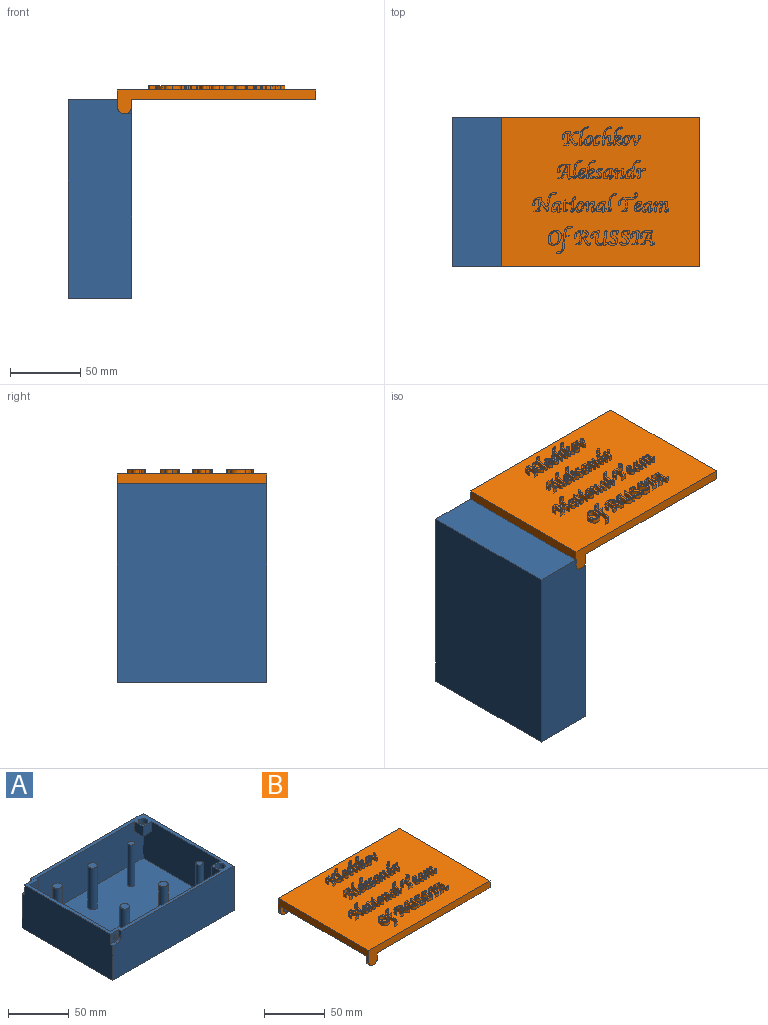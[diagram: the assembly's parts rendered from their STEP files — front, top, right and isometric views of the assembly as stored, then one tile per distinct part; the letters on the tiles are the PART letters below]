
ASSEMBLY  parts=2 mates=1
PART A: 53 faces, bbox 141x106x45 mm
  f0: plane 106x45mm, normal (-1,0,0), area 4710.1mm2, adj f1,f10,f11,f12,f29,f32,f47,f50
  f1: plane 141x106mm, normal (0,0,1), area 1548.2mm2, adj f0,f2,f3,f4,f5,f6,f7,f8
  f2: plane 100x42mm, normal (1,0,0), area 4137.9mm2, adj f1,f3,f4,f35,f36,f38,f43,f44
  f3: plane 135x42mm, normal (0,-1,0), area 5469.5mm2, adj f1,f2,f9,f26,f37,f38,f44,f45
  f4: plane 135x42mm, normal (0,1,0), area 5469.5mm2, adj f1,f2,f9,f27,f38,f39,f41,f42
  f5: cylinder r=4mm len=8mm, axis (0,0,-1), area 125.7mm2, adj f1,f40
  f6: plane 10x10mm, normal (0,1,0), area 100mm2, adj f1,f9,f27,f39
  f7: plane 10x10mm, normal (0,-1,0), area 100mm2, adj f1,f9,f26,f37
  f8: cylinder r=4mm len=8mm, axis (0,0,-1), area 125.7mm2, adj f1,f28
  f9: plane 100x42mm, normal (-1,0,0), area 4000mm2, adj f1,f3,f4,f6,f7,f37,f38,f39
  f10: plane 141x45mm, normal (0,1,0), area 6250.8mm2, adj f0,f1,f12,f13,f32,f33,f34
  f11: plane 141x45mm, normal (0,-1,0), area 6250.8mm2, adj f0,f1,f12,f13,f29,f30,f31
  f12: plane 141x106mm, normal (0,0,-1), area 14946mm2, adj f0,f10,f11,f13
  f13: plane 106x45mm, normal (1,0,0), area 4770mm2, adj f1,f10,f11,f12
  f14: plane 7.9x7.9mm, normal (0,0,1), area 49mm2, adj f15
  f15: cylinder r=3.95mm len=42mm, axis (0,0,-1), area 1042.4mm2, adj f14,f38
  f16: plane 7.9x7.9mm, normal (0,0,1), area 49mm2, adj f17
  f17: cylinder r=3.95mm len=42mm, axis (0,0,-1), area 1042.4mm2, adj f16,f38
  f18: plane 7.9x7.9mm, normal (0,0,1), area 49mm2, adj f19
  f19: cylinder r=3.95mm len=42mm, axis (0,0,-1), area 1042.4mm2, adj f18,f38
  f20: plane 5.9x5.9mm, normal (0,0,1), area 27.3mm2, adj f21
  f21: cylinder r=2.95mm len=42mm, axis (0,0,-1), area 778.5mm2, adj f20,f38
  f22: plane 7.9x7.9mm, normal (0,0,1), area 49mm2, adj f23
  f23: cylinder r=3.95mm len=42mm, axis (0,0,-1), area 1042.4mm2, adj f22,f38
  f24: plane 5.9x5.9mm, normal (0,0,1), area 27.3mm2, adj f25
  f25: cylinder r=2.95mm len=42mm, axis (0,0,-1), area 778.5mm2, adj f24,f38
  f26: plane 10x10mm, normal (-1,0,0), area 100mm2, adj f1,f3,f7,f37
  f27: plane 10x10mm, normal (-1,0,0), area 100mm2, adj f1,f4,f6,f39
  f28: plane 8x8mm, normal (0,0,1), area 50.3mm2, adj f8
  f29: plane 5.33x3mm, normal (0,0,1), area 16mm2, adj f0,f11,f30,f50
  f30: cylinder r=5mm len=5.13mm, axis (0,-1,0), area 23mm2, adj f11,f29,f31,f50
  f31: plane 4.86x3mm, normal (-1,0,-0.03), area 14.6mm2, adj f1,f11,f30,f50
  f32: plane 5.33x3mm, normal (0,0,1), area 16mm2, adj f0,f10,f34,f47
  f33: plane 4.86x3mm, normal (-1,0,-0.03), area 14.6mm2, adj f1,f10,f34,f47
  f34: cylinder r=5mm len=5.13mm, axis (0,1,0), area 23mm2, adj f10,f32,f33,f47
  f35: plane 10.34x10.31mm, normal (0,-1,0), area 100.5mm2, adj f1,f2,f44,f45,f46
  f36: plane 10.34x10.31mm, normal (0,1,0), area 100.5mm2, adj f1,f2,f41,f42,f43
  f37: plane 10x10mm, normal (0,0,-1), area 100mm2, adj f3,f7,f9,f26
  f38: plane 135x100mm, normal (0,0,1), area 13249.3mm2, adj f2,f3,f4,f9,f15,f17,f19,f21
  f39: plane 10x10mm, normal (0,0,-1), area 100mm2, adj f4,f6,f9,f27
  f40: plane 8x8mm, normal (0,0,1), area 50.3mm2, adj f5
  f41: plane 5x3mm, normal (1,0,0), area 15mm2, adj f1,f4,f36,f42
  f42: cylinder r=5.34mm len=5.34mm, axis (0,1,0), area 25.2mm2, adj f4,f36,f41,f43
  f43: plane 4.97x3mm, normal (0,0,-1), area 14.9mm2, adj f2,f4,f36,f42
  f44: plane 4.97x3mm, normal (0,0,-1), area 14.9mm2, adj f2,f3,f35,f45
  f45: cylinder r=5.34mm len=5.34mm, axis (0,-1,0), area 25.2mm2, adj f3,f35,f44,f46
  f46: plane 5x3mm, normal (1,0,0), area 15mm2, adj f1,f3,f35,f45
  f47: plane 10x9.99mm, normal (0,1,0), area 81.7mm2, adj f0,f1,f32,f33,f34,f49
  f48: plane 4x4mm, normal (0,1,0), area 12.6mm2, adj f49
  f49: cylinder r=2mm len=4mm, axis (0,1,0), area 18.8mm2, adj f47,f48
  f50: plane 10x9.99mm, normal (0,-1,0), area 81.7mm2, adj f0,f1,f29,f30,f31,f52
  f51: plane 4x4mm, normal (0,-1,0), area 12.6mm2, adj f52
  f52: cylinder r=2mm len=4mm, axis (0,-1,0), area 18.8mm2, adj f50,f51
PART B: 222 faces, bbox 141x106x20 mm
  f0: plane 141x106mm, normal (0,0,1), area 13851.5mm2, adj f6,f7,f8,f11,f32,f33,f34,f35
  f1: plane 100x3mm, normal (0,0,-1), area 300mm2, adj f8,f20,f22,f27
  f2: plane 131.14x106mm, normal (0,0,-1), area 1297.1mm2, adj f3,f6,f7,f9,f11,f13,f14,f16
  f3: plane 11.79x4mm, normal (-1,0,0), area 47.1mm2, adj f2,f22,f23,f26
  f4: plane 3x0.66mm, normal (0,0,-1), area 2mm2, adj f6,f10,f19,f20
  f5: plane 3x0.66mm, normal (0,0,-1), area 2mm2, adj f7,f12,f18,f22
  f6: plane 141x16.99mm, normal (0,1,0), area 1075.9mm2, adj f0,f2,f4,f8,f9,f10,f11,f19
  f7: plane 141x16.99mm, normal (0,-1,0), area 1075.9mm2, adj f0,f2,f5,f8,f11,f12,f13,f18
  f8: plane 106x12mm, normal (-1,0,0), area 772mm2, adj f0,f1,f6,f7,f18,f19,f20,f22
  f9: plane 4.86x3mm, normal (1,0,0.03), area 14.6mm2, adj f2,f6,f10,f20
  f10: cylinder r=5mm len=5.13mm, axis (0,-1,0), area 23mm2, adj f4,f6,f9,f20
  f11: plane 106x7mm, normal (1,0,0), area 742mm2, adj f0,f2,f6,f7
  f12: cylinder r=5mm len=5.13mm, axis (0,1,0), area 23mm2, adj f5,f7,f13,f22
  f13: plane 4.86x3mm, normal (1,0,0.03), area 14.6mm2, adj f2,f7,f12,f22
  f14: cylinder r=4mm len=8mm, axis (0,0,-1), area 125.7mm2, adj f2,f15
  f15: plane 8x8mm, normal (0,0,-1), area 50.3mm2, adj f14
  f16: cylinder r=4mm len=8mm, axis (0,0,-1), area 125.7mm2, adj f2,f17
  f17: plane 8x8mm, normal (0,0,-1), area 50.3mm2, adj f16
  f18: cylinder r=5mm len=4.99mm, axis (0,1,0), area 22.6mm2, adj f5,f7,f8,f22
  f19: cylinder r=5mm len=4.99mm, axis (0,1,0), area 22.6mm2, adj f4,f6,f8,f20
  f20: plane 124.82x13.99mm, normal (0,-1,0), area 563.6mm2, adj f1,f2,f4,f8,f9,f10,f19,f21
  f21: plane 11.79x4mm, normal (-1,0,0), area 47.1mm2, adj f2,f20,f23,f24
  f22: plane 124.82x13.99mm, normal (0,1,0), area 563.6mm2, adj f1,f2,f3,f5,f8,f12,f13,f18
  f23: plane 135x100mm, normal (0,0,-1), area 13189.2mm2, adj f3,f20,f21,f22,f24,f25,f26,f27
  f24: plane 13.19x4mm, normal (0,-1,0), area 52.7mm2, adj f2,f21,f23,f25
  f25: plane 76.43x4mm, normal (-1,0,0), area 305.7mm2, adj f2,f23,f24,f26
  f26: plane 13.19x4mm, normal (0,1,0), area 52.7mm2, adj f2,f3,f23,f25
  f27: plane 100x4mm, normal (1,0,0), area 400mm2, adj f1,f20,f22,f23
  f28: plane 4x4mm, normal (0,1,0), area 12.6mm2, adj f29
  f29: cylinder r=2mm len=4mm, axis (0,-1,0), area 18.8mm2, adj f22,f28
  f30: plane 4x4mm, normal (0,-1,0), area 12.6mm2, adj f31
  f31: cylinder r=2mm len=4mm, axis (0,1,0), area 18.8mm2, adj f20,f30
  f32: plane 3x0.46mm, normal (0,-1,0), area 1.4mm2, adj f0,f33,f45,f46
  f33: extruded ~9.8x6.28mm, area 97.6mm2, adj f0,f32,f34,f46
  f34: plane 3.88x3mm, normal (1,-0.07,0), area 11.7mm2, adj f0,f33,f35,f46
  f35: extruded ~5.75x5.6mm, area 34.6mm2, adj f0,f34,f36,f46
  f36: extruded ~3.07x3mm, area 14.9mm2, adj f0,f35,f37,f46
  f37: plane 5.75x3mm, normal (-1,0.06,0), area 17.3mm2, adj f0,f36,f38,f46
  f38: extruded ~3x1.94mm, area 6.8mm2, adj f0,f37,f39,f46
  f39: plane 3x0.86mm, normal (0,1,0), area 2.6mm2, adj f0,f38,f40,f46
  f40: plane 3x1.02mm, normal (-0.76,0.65,0), area 4.1mm2, adj f0,f39,f41,f46
  f41: plane 3.21x3mm, normal (0,-1,0), area 9.6mm2, adj f0,f40,f42,f46
  f42: plane 3x1.02mm, normal (0.77,-0.64,0), area 4mm2, adj f0,f41,f43,f46
  f43: plane 3x1.31mm, normal (0,1,0), area 3.9mm2, adj f0,f42,f44,f46
  f44: extruded ~3x1.68mm, area 6.4mm2, adj f0,f43,f45,f46
  f45: plane 3x2.26mm, normal (1,-0.06,0), area 6.8mm2, adj f0,f32,f44,f46
  f46: plane 12.18x10.17mm, normal (0,0,1), area 39.2mm2, adj f32,f33,f34,f35,f36,f37,f38,f39
  f47: extruded ~3x0.07mm, area 0.2mm2, adj f0,f48,f49,f50
  f48: extruded ~3x0.05mm, area 0.2mm2, adj f0,f47,f49,f50
  f49: extruded ~13.13x6.12mm, area 104.5mm2, adj f0,f47,f48,f50
  f50: plane 13.43x6.6mm, normal (0,0,1), area 18.7mm2, adj f47,f48,f49
  f51: extruded ~13.11x6.1mm, area 112.6mm2, adj f0,f52
  f52: plane 13.43x6.68mm, normal (0,0,1), area 18.5mm2, adj f51
  f53: extruded ~5.21x3.05mm, area 29.6mm2, adj f54,f56,f57
  f54: extruded ~3.34x3mm, area 10.6mm2, adj f53,f56,f57
  f55: extruded ~7.34x5.72mm, area 62.3mm2, adj f0,f56
  f56: plane 7.51x5.83mm, normal (0,0,1), area 19.4mm2, adj f53,f54,f55
  f57: plane 5.28x3.18mm, normal (0,0,1), area 12.5mm2, adj f53,f54
  f58: extruded ~7.3x5.23mm, area 83.1mm2, adj f0,f59
  f59: plane 7.41x5.36mm, normal (0,0,1), area 15mm2, adj f58
  f60: extruded ~13.06x6.77mm, area 184.9mm2, adj f0,f61
  f61: plane 13.49x7.45mm, normal (0,0,1), area 32.1mm2, adj f60
  f62: extruded ~5.21x3.05mm, area 29.6mm2, adj f63,f65,f66
  f63: extruded ~3.34x3mm, area 10.6mm2, adj f62,f65,f66
  f64: extruded ~7.34x5.72mm, area 62.3mm2, adj f0,f65
  f65: plane 7.51x5.83mm, normal (0,0,1), area 19.4mm2, adj f62,f63,f64
  f66: plane 5.28x3.18mm, normal (0,0,1), area 12.5mm2, adj f62,f63
  f67: extruded ~3x2.62mm, area 23.7mm2, adj f69,f70
  f68: extruded ~12.89x6.37mm, area 156.4mm2, adj f0,f69
  f69: plane 13.2x6.64mm, normal (0,0,1), area 28mm2, adj f67,f68
  f70: plane 2.67x2.54mm, normal (0,0,1), area 3.9mm2, adj f67
  f71: extruded ~3x2.62mm, area 23.7mm2, adj f73,f74
  f72: extruded ~12.89x6.37mm, area 156.4mm2, adj f0,f73
  f73: plane 13.2x6.64mm, normal (0,0,1), area 28mm2, adj f71,f72
  f74: plane 2.67x2.54mm, normal (0,0,1), area 3.9mm2, adj f71
  f75: extruded ~5.21x3.05mm, area 29.6mm2, adj f76,f78,f79
  f76: extruded ~3.34x3mm, area 10.6mm2, adj f75,f78,f79
  f77: extruded ~7.34x5.72mm, area 62.3mm2, adj f0,f78
  f78: plane 7.51x5.83mm, normal (0,0,1), area 19.4mm2, adj f75,f76,f77
  f79: plane 5.28x3.18mm, normal (0,0,1), area 12.5mm2, adj f75,f76
  f80: extruded ~13.11x6.1mm, area 112.6mm2, adj f0,f81
  f81: plane 13.43x6.68mm, normal (0,0,1), area 18.5mm2, adj f80
  f82: extruded ~7.38x7.14mm, area 98.2mm2, adj f0,f83
  f83: plane 7.59x7.39mm, normal (0,0,1), area 17.4mm2, adj f82
  f84: extruded ~10.22x3.42mm, area 52.6mm2, adj f0,f85,f94,f95
  f85: extruded ~9.01x8.57mm, area 93.9mm2, adj f0,f84,f86,f95
  f86: plane 3x1.05mm, normal (0,1,0), area 3.1mm2, adj f0,f85,f87,f95
  f87: plane 3x0.99mm, normal (-0.74,0.67,0), area 4mm2, adj f0,f86,f88,f95
  f88: plane 3.2x3mm, normal (0,-1,0), area 9.6mm2, adj f0,f87,f89,f95
  f89: plane 3x0.99mm, normal (0.76,-0.66,0), area 3.9mm2, adj f0,f88,f90,f95
  f90: plane 3x1.23mm, normal (0,1,0), area 3.7mm2, adj f0,f89,f91,f95
  f91: extruded ~3x2.23mm, area 8.1mm2, adj f0,f90,f94,f95
  f92: extruded ~4.34x3mm, area 28.7mm2, adj f93,f95,f96
  f93: plane 3x2.63mm, normal (0,1,0), area 7.9mm2, adj f92,f95,f96
  f94: plane 3x2.65mm, normal (0,-1,0), area 7.9mm2, adj f0,f84,f91,f95
  f95: plane 10.46x10.43mm, normal (0,0,1), area 37.6mm2, adj f84,f85,f86,f87,f88,f89,f90,f91
  f96: plane 4.37x2.78mm, normal (0,0,1), area 7.6mm2, adj f92,f93
  f97: extruded ~4.54x3.15mm, area 25.4mm2, adj f0,f99,f100
  f98: extruded ~3x2.49mm, area 22.7mm2, adj f100,f101
  f99: extruded ~4.9x4.83mm, area 58.8mm2, adj f0,f97,f100
  f100: plane 7.62x5.02mm, normal (0,0,1), area 18.5mm2, adj f97,f98,f99
  f101: plane 2.52x2.42mm, normal (0,0,1), area 4.1mm2, adj f98
  f102: extruded ~4.54x3.15mm, area 25.4mm2, adj f0,f104,f105
  f103: extruded ~3x2.49mm, area 22.7mm2, adj f105,f106
  f104: extruded ~4.9x4.83mm, area 58.8mm2, adj f0,f102,f105
  f105: plane 7.62x5.02mm, normal (0,0,1), area 18.5mm2, adj f102,f103,f104
  f106: plane 2.52x2.42mm, normal (0,0,1), area 4.1mm2, adj f103
  f107: extruded ~7.44x4.89mm, area 83.2mm2, adj f0,f108
  f108: plane 7.56x5.18mm, normal (0,0,1), area 15.5mm2, adj f107
  f109: extruded ~7.45x7.32mm, area 96mm2, adj f0,f111
  f110: extruded ~4.9x3.37mm, area 39.2mm2, adj f111,f112
  f111: plane 7.59x7.42mm, normal (0,0,1), area 25.5mm2, adj f109,f110
  f112: plane 4.96x3.42mm, normal (0,0,1), area 11.1mm2, adj f110
  f113: extruded ~7.45x7.32mm, area 96mm2, adj f0,f115
  f114: extruded ~4.9x3.37mm, area 39.2mm2, adj f115,f116
  f115: plane 7.59x7.42mm, normal (0,0,1), area 25.5mm2, adj f113,f114
  f116: plane 4.96x3.42mm, normal (0,0,1), area 11.1mm2, adj f114
  f117: extruded ~7.45x7.32mm, area 96mm2, adj f0,f119
  f118: extruded ~4.9x3.37mm, area 39.2mm2, adj f119,f120
  f119: plane 7.59x7.42mm, normal (0,0,1), area 25.5mm2, adj f117,f118
  f120: plane 4.96x3.42mm, normal (0,0,1), area 11.1mm2, adj f118
  f121: extruded ~7.45x7.32mm, area 96mm2, adj f0,f123
  f122: extruded ~4.9x3.37mm, area 39.2mm2, adj f123,f124
  f123: plane 7.59x7.42mm, normal (0,0,1), area 25.5mm2, adj f121,f122
  f124: plane 4.96x3.42mm, normal (0,0,1), area 11.1mm2, adj f122
  f125: extruded ~8.1x7.35mm, area 138.6mm2, adj f0,f126
  f126: plane 8.26x7.68mm, normal (0,0,1), area 25.8mm2, adj f125
  f127: extruded ~8.1x7.35mm, area 138.6mm2, adj f0,f128
  f128: plane 8.26x7.68mm, normal (0,0,1), area 25.8mm2, adj f127
  f129: extruded ~4.82x3.26mm, area 38.3mm2, adj f131,f132
  f130: extruded ~13.36x10.38mm, area 140.8mm2, adj f0,f131
  f131: plane 13.52x10.64mm, normal (0,0,1), area 31.9mm2, adj f129,f130
  f132: plane 4.9x3.33mm, normal (0,0,1), area 10.4mm2, adj f129
  f133: extruded ~7.09x6.61mm, area 95.1mm2, adj f0,f134
  f134: plane 7.43x6.93mm, normal (0,0,1), area 16.1mm2, adj f133
  f135: extruded ~3x1.83mm, area 9.5mm2, adj f0,f136,f143,f144
  f136: plane 3x1.33mm, normal (-1,0.08,0), area 4mm2, adj f0,f135,f137,f144
  f137: plane 3x0.6mm, normal (0,1,0), area 1.8mm2, adj f0,f136,f138,f144
  f138: plane 3x0.85mm, normal (-0.71,0.71,0), area 3.6mm2, adj f0,f137,f139,f144
  f139: plane 3x1.33mm, normal (0,-1,0), area 4mm2, adj f0,f138,f140,f144
  f140: extruded ~6.18x3.12mm, area 52.7mm2, adj f0,f139,f141,f144
  f141: plane 3x2.24mm, normal (0,-1,0), area 6.7mm2, adj f0,f140,f142,f144
  f142: plane 3x0.86mm, normal (0.7,-0.71,0), area 3.6mm2, adj f0,f141,f143,f144
  f143: plane 3x3mm, normal (0,1,0), area 9mm2, adj f0,f135,f142,f144
  f144: plane 8.97x5.81mm, normal (0,0,1), area 16.2mm2, adj f135,f136,f137,f138,f139,f140,f141,f142
  f145: extruded ~3x2.68mm, area 23.1mm2, adj f0,f146
  f146: plane 2.77x2.47mm, normal (0,0,1), area 3.3mm2, adj f145
  f147: extruded ~7.45x3.8mm, area 75mm2, adj f0,f148
  f148: plane 7.67x3.96mm, normal (0,0,1), area 12.9mm2, adj f147
  f149: plane 3x0.79mm, normal (0,1,0), area 2.4mm2, adj f0,f150,f156,f157
  f150: plane 3x1.12mm, normal (-0.73,0.68,0), area 4.6mm2, adj f0,f149,f151,f157
  f151: plane 3.81x3mm, normal (0,-1,0), area 11.4mm2, adj f0,f150,f152,f157
  f152: plane 3x1.12mm, normal (0.74,-0.67,0), area 4.6mm2, adj f0,f151,f153,f157
  f153: plane 3x1.51mm, normal (0,1,0), area 4.5mm2, adj f0,f152,f154,f157
  f154: extruded ~16.27x13.69mm, area 192.4mm2, adj f0,f153,f155,f157
  f155: plane 3x0.05mm, normal (-0.68,-0.73,0), area 0.2mm2, adj f0,f154,f156,f157
  f156: extruded ~7.63x3mm, area 24.3mm2, adj f0,f149,f155,f157
  f157: plane 16.62x13.82mm, normal (0,0,1), area 54.6mm2, adj f149,f150,f151,f152,f153,f154,f155,f156
  f158: plane 3x1.25mm, normal (0,1,0), area 3.8mm2, adj f0,f159,f164,f165
  f159: plane 3x0.98mm, normal (-0.79,0.61,0), area 3.7mm2, adj f0,f158,f160,f165
  f160: plane 4.11x3mm, normal (0,-1,0), area 12.3mm2, adj f0,f159,f161,f165
  f161: plane 3x0.98mm, normal (0.84,-0.55,0), area 3.5mm2, adj f0,f160,f162,f165
  f162: plane 3x1.46mm, normal (0,1,0), area 4.4mm2, adj f0,f161,f163,f165
  f163: extruded ~13.29x12.4mm, area 136.1mm2, adj f0,f162,f164,f165
  f164: extruded ~7.83x3mm, area 24.4mm2, adj f0,f158,f163,f165
  f165: plane 13.8x13.48mm, normal (0,0,1), area 36.9mm2, adj f158,f159,f160,f161,f162,f163,f164
  f166: extruded ~10.9x7.53mm, area 221.8mm2, adj f0,f167
  f167: plane 11.36x7.86mm, normal (0,0,1), area 33.3mm2, adj f166
  f168: extruded ~9.06x6.17mm, area 72.7mm2, adj f170,f171
  f169: extruded ~10.56x9.37mm, area 96.1mm2, adj f0,f170
  f170: plane 10.65x9.48mm, normal (0,0,1), area 35.2mm2, adj f168,f169
  f171: plane 9.17x6.26mm, normal (0,0,1), area 44mm2, adj f168
  f172: extruded ~5.15x3.82mm, area 22.8mm2, adj f0,f173,f181,f182
  f173: extruded ~6.4x6.14mm, area 35.7mm2, adj f0,f172,f174,f182
  f174: plane 3x0.59mm, normal (0,1,0), area 1.8mm2, adj f0,f173,f175,f182
  f175: plane 3x0.8mm, normal (-0.75,0.66,0), area 3.2mm2, adj f0,f174,f176,f182
  f176: plane 3x1.29mm, normal (0,-1,0), area 3.9mm2, adj f0,f175,f177,f182
  f177: extruded ~10.93x4.28mm, area 40.1mm2, adj f0,f176,f178,f182
  f178: extruded ~12.07x6.56mm, area 52.2mm2, adj f0,f177,f179,f182
  f179: plane 3x2.09mm, normal (0,-1,0), area 6.3mm2, adj f0,f178,f180,f182
  f180: plane 3x0.8mm, normal (0.76,-0.65,0), area 3.2mm2, adj f0,f179,f181,f182
  f181: plane 3x2.78mm, normal (0,1,0), area 8.3mm2, adj f0,f172,f180,f182
  f182: plane 19.36x11.47mm, normal (0,0,1), area 31.1mm2, adj f172,f173,f174,f175,f176,f177,f178,f179
  f183: extruded ~11.61x10.45mm, area 115.4mm2, adj f0,f184,f189,f191
  f184: extruded ~8.17x3.09mm, area 42.4mm2, adj f0,f183,f185,f191
  f185: plane 3x0.83mm, normal (0,1,0), area 2.5mm2, adj f0,f184,f186,f191
  f186: plane 3x0.99mm, normal (-0.82,0.57,0), area 3.6mm2, adj f0,f185,f187,f191
  f187: plane 3.36x3mm, normal (0,-1,0), area 10.1mm2, adj f0,f186,f188,f191
  f188: plane 3x0.99mm, normal (0.85,-0.52,0), area 3.5mm2, adj f0,f187,f189,f191
  f189: plane 3x1.16mm, normal (0,1,0), area 3.5mm2, adj f0,f183,f188,f191
  f190: extruded ~4.26x3.25mm, area 36.6mm2, adj f191,f192
  f191: plane 11.79x10.67mm, normal (0,0,1), area 42.7mm2, adj f183,f184,f185,f186,f187,f188,f189,f190
  f192: plane 4.38x3.35mm, normal (0,0,1), area 10.4mm2, adj f190
  f193: extruded ~12.02x10.39mm, area 202.3mm2, adj f0,f194
  f194: plane 12.45x11.03mm, normal (0,0,1), area 43mm2, adj f193
  f195: extruded ~8.91x5.99mm, area 62.9mm2, adj f0,f196,f201,f202
  f196: extruded ~7.74x3mm, area 39.3mm2, adj f0,f195,f197,f202
  f197: plane 3x1.2mm, normal (0,1,0), area 3.6mm2, adj f0,f196,f198,f202
  f198: plane 3x1.14mm, normal (-0.76,0.65,0), area 4.5mm2, adj f0,f197,f199,f202
  f199: plane 4.1x3mm, normal (0,-1,0), area 12.3mm2, adj f0,f198,f200,f202
  f200: plane 3x1.14mm, normal (0.73,-0.69,0), area 4.7mm2, adj f0,f199,f201,f202
  f201: plane 3x1.78mm, normal (0,1,0), area 5.3mm2, adj f0,f195,f200,f202
  f202: plane 10.19x6.28mm, normal (0,0,1), area 25.2mm2, adj f195,f196,f197,f198,f199,f200,f201
  f203: extruded ~9.29x3.91mm, area 46.5mm2, adj f0,f204,f205
  f204: extruded ~10.58x7.09mm, area 95.3mm2, adj f0,f203,f205
  f205: plane 10.72x7.27mm, normal (0,0,1), area 29.4mm2, adj f203,f204
  f206: extruded ~9.29x3.91mm, area 46.5mm2, adj f0,f207,f208
  f207: extruded ~10.58x7.09mm, area 95.3mm2, adj f0,f206,f208
  f208: plane 10.72x7.27mm, normal (0,0,1), area 29.4mm2, adj f206,f207
  f209: extruded ~10.22x3.42mm, area 52.6mm2, adj f0,f210,f219,f220
  f210: extruded ~9.01x8.57mm, area 93.9mm2, adj f0,f209,f211,f220
  f211: plane 3x1.05mm, normal (0,1,0), area 3.1mm2, adj f0,f210,f212,f220
  f212: plane 3x0.99mm, normal (-0.74,0.67,0), area 4mm2, adj f0,f211,f213,f220
  f213: plane 3.2x3mm, normal (0,-1,0), area 9.6mm2, adj f0,f212,f214,f220
  f214: plane 3x0.99mm, normal (0.76,-0.66,0), area 3.9mm2, adj f0,f213,f215,f220
  f215: plane 3x1.23mm, normal (0,1,0), area 3.7mm2, adj f0,f214,f216,f220
  f216: extruded ~3x2.23mm, area 8.1mm2, adj f0,f215,f219,f220
  f217: extruded ~4.34x3mm, area 28.7mm2, adj f218,f220,f221
  f218: plane 3x2.63mm, normal (0,1,0), area 7.9mm2, adj f217,f220,f221
  f219: plane 3x2.65mm, normal (0,-1,0), area 7.9mm2, adj f0,f209,f216,f220
  f220: plane 10.46x10.43mm, normal (0,0,1), area 37.6mm2, adj f209,f210,f211,f212,f213,f214,f215,f216
  f221: plane 4.37x2.78mm, normal (0,0,1), area 7.6mm2, adj f217,f218
PLACE A rot(axis=(0,1,0),90deg) t=(-294.11,-34.4,22.09)mm
PLACE B rot(axis=(0.08,0,-1),0deg) t=(-166.11,-34.4,70.09)mm
MATE revolute B.f10 <-> A.f30  axis (0,1,0) through (-254.11,-84.4,110.09)mm
